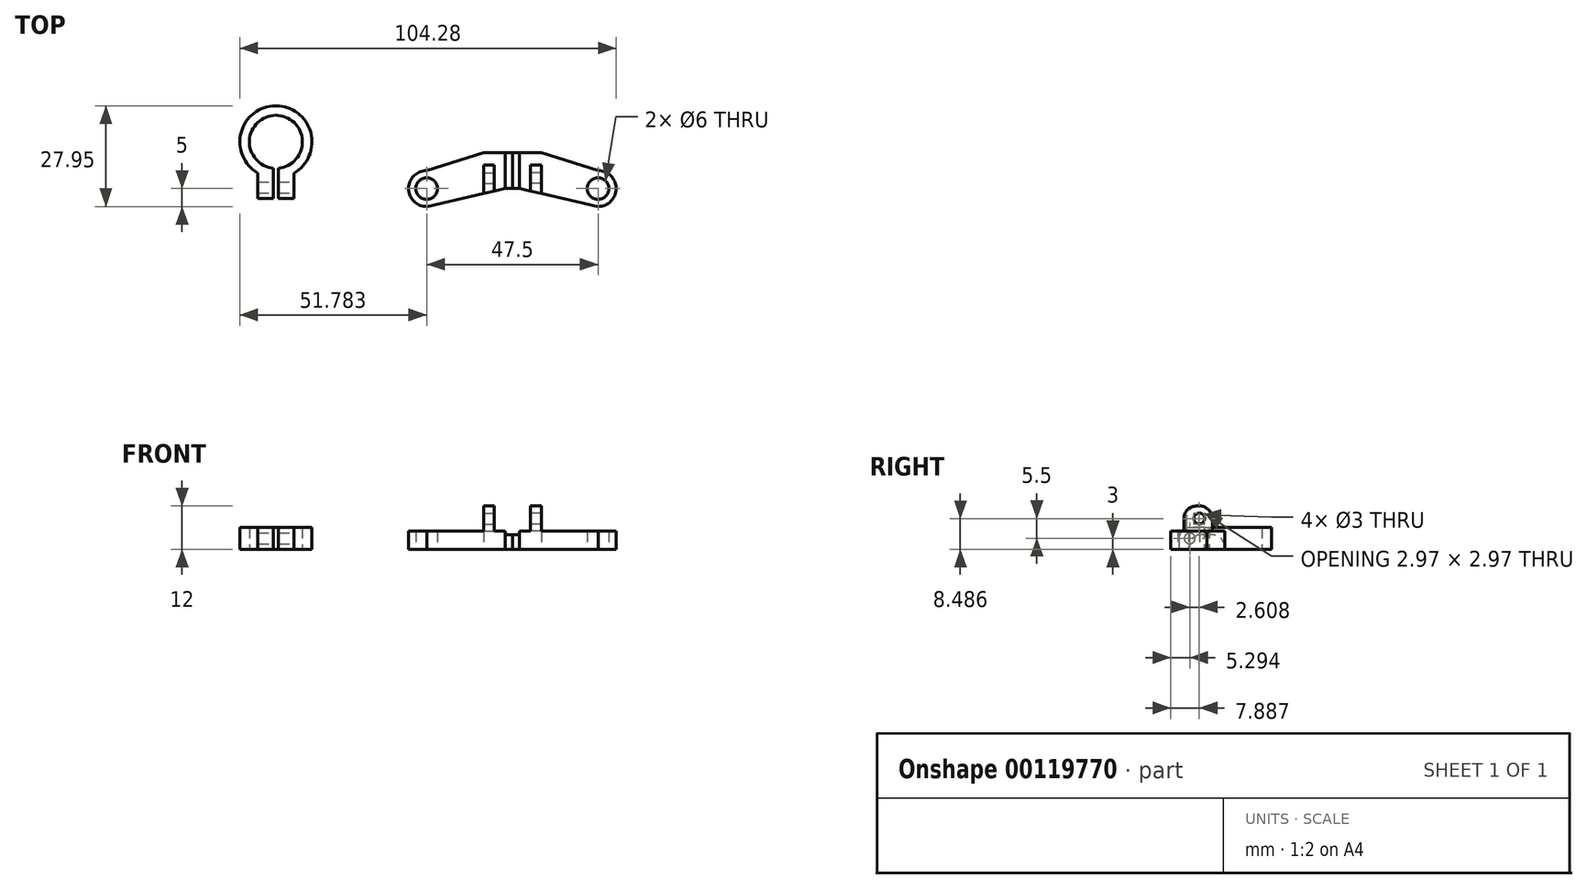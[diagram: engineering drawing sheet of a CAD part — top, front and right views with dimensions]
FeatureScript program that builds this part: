
annotation { "Feature Type Name" : "Feature", "Feature Type Description" : "" }
export const myFeature = defineFeature(function(context is Context, id is Id, definition is map)
    precondition{}
    {
        {
            var Q0;
            Q0=qCreatedBy(makeId("Top.planeOp"),FACE);
            var sketch = newSketch(context, id + "F0", { "sketchPlane" : qUnion([Q0])});
            skCircle(sketch, "E0", {"center": v(-31.45, 17.95) * mm, "radius": 7.35 * mm});
            skCircle(sketch, "E1", {"center": v(-31.45, 17.95) * mm, "radius": 10 * mm});
            skLineSegment(sketch, "E2", {"start": v(-26.45, 9.3) * mm, "end": v(-26.45, 2.3) * mm});
            skLineSegment(sketch, "E3", {"start": v(-26.45, 2.3) * mm, "end": v(-36.45, 2.3) * mm});
            skLineSegment(sketch, "E4", {"start": v(-36.45, 2.3) * mm, "end": v(-36.45, 9.3) * mm});
            skLineSegment(sketch, "E5", {"start": v(-32.15, 2.3) * mm, "end": v(-32.15, 10.64) * mm});
            skLineSegment(sketch, "E6", {"start": v(-30.75, 2.3) * mm, "end": v(-30.75, 10.64) * mm});
            skSolve(sketch);
        }
        {
            var Q0;
            {var subQ0=sQuery(id+"F0.wireOp",EDGE,"E2");Q0=makeQuery(id+"F0.imprint","IMPRINT",FACE,{"disambiguationData":[TD([[makeQuery(id+"F0.imprint","IMPRINT",EDGE,{"derivedFrom":subQ0}),-1.0]])]});}
            var Q1;
            {var subQ0=sQuery(id+"F0.wireOp",EDGE,"E4");Q1=makeQuery(id+"F0.imprint","IMPRINT",FACE,{"disambiguationData":[TD([[makeQuery(id+"F0.imprint","IMPRINT",EDGE,{"derivedFrom":subQ0}),-1.0]])]});}
            var Q2;
            {var subQ3=sQuery(id+"F0.wireOp",EDGE,"E5");var subQ4=sQuery(id+"F0.wireOp",EDGE,"E0");var subQ5=makeQuery(id+"F0.imprint","INTERSECT",VERTEX,{"derivedFrom":[subQ4,subQ3]});Q2=makeQuery(id+"F0.imprint","IMPRINT",FACE,{"disambiguationData":[TD([[makeQuery(id+"F0.imprint","IMPRINT",EDGE,{"disambiguationData":[TD([[subQ5,1.0]])],"derivedFrom":subQ4}),-1.0]])]});}
            extrude(context, id + "F1", {"entities" : qUnion([Q0, Q1, Q2]), "depth" : 6 * mm});
        }
        {
            var Q0;
            Q0=makeQuery(id+"F1.opExtrude","SWEPT_FACE",FACE,{"disambiguationData":[OSD([sQuery(id+"F0.wireOp",EDGE,"E2")])]});
            var sketch = newSketch(context, id + "F2", { "sketchPlane" : qUnion([Q0])});
            skPoint(sketch, "E7", {"position": v(5.3, 3) * mm});
            skSolve(sketch);
        }
        {
            var Q0;
            Q0=sQuery(id+"F2.wireOp",VERTEX,"E7");
            var Q1;
            Q1=makeQuery(id+"F1.opExtrude","SWEPT_BODY",BODY,{"disambiguationData":[OSD([sQuery(id+"F0.wireOp",EDGE,"E0"),sQuery(id+"F0.wireOp",EDGE,"E1"),sQuery(id+"F0.wireOp",EDGE,"E2"),sQuery(id+"F0.wireOp",EDGE,"E3"),sQuery(id+"F0.wireOp",EDGE,"E4")])]});
            hole(context, id + "F3", {"style" : HoleStyle.SIMPLE, "endStyle" : HoleEndStyle.THROUGH, "holeDiameter" : 3 * mm, "locations" : qUnion([Q0]), "scope" : qUnion([Q1]), "isTappedThrough" : true});
        }
        {
            var Q0;
            Q0=qCreatedBy(makeId("Top.planeOp"),FACE);
            var sketch = newSketch(context, id + "F4", { "sketchPlane" : qUnion([Q0])});
            skCircle(sketch, "E8", {"center": v(10.33, 5) * mm, "radius": 3 * mm});
            skLineSegment(sketch, "E9.left", {"start": v(5.33, 10) * mm, "end": v(5.33, 0) * mm});
            skPoint(sketch, "E10", {"position": v(10.33, 0) * mm});
            skPoint(sketch, "E11", {"position": v(34.08, 5) * mm});
            skLineSegment(sketch, "E12", {"start": v(34.08, 5) * mm, "end": v(32.08, 5) * mm});
            skLineSegment(sketch, "E13", {"start": v(32.08, 5) * mm, "end": v(10.33, 0) * mm});
            skPoint(sketch, "E14", {"position": v(29.08, 5) * mm});
            skPoint(sketch, "E15", {"position": v(26.08, 5) * mm});
            skLineSegment(sketch, "E16", {"start": v(26.08, 5) * mm, "end": v(26.08, 15) * mm});
            skLineSegment(sketch, "E17", {"start": v(34.08, 15) * mm, "end": v(26.08, 15) * mm});
            skLineSegment(sketch, "E18", {"start": v(29.08, 5) * mm, "end": v(29.08, 15) * mm});
            skPoint(sketch, "E19", {"position": v(32.08, 15) * mm});
            skLineSegment(sketch, "E20", {"start": v(32.08, 5) * mm, "end": v(32.08, 5) * mm});
            skPoint(sketch, "E21", {"position": v(10.33, 10) * mm});
            skLineSegment(sketch, "E22", {"start": v(32.08, 15) * mm, "end": v(32.08, 5) * mm});
            skLineSegment(sketch, "E23", {"start": v(5.33, 10) * mm, "end": v(10.33, 10) * mm});
            skLineSegment(sketch, "E24", {"start": v(5.33, 0) * mm, "end": v(10.33, 0) * mm});
            skLineSegment(sketch, "E25", {"start": v(34.08, 5) * mm, "end": v(34.08, 15) * mm});
            skLineSegment(sketch, "E26", {"start": v(10.33, 10) * mm, "end": v(26.08, 15) * mm});
            skPoint(sketch, "E27", {"position": v(26.08, 11.5) * mm});
            skLineSegment(sketch, "E28", {"start": v(26.08, 11.5) * mm, "end": v(29.08, 11.5) * mm});
            skLineSegment(sketch, "E29", {"start": v(26.08, 5) * mm, "end": v(26.08, 3.62) * mm});
            skLineSegment(sketch, "E30", {"start": v(29.08, 5) * mm, "end": v(29.08, 4.31) * mm});
            skSolve(sketch);
        }
        {
            var Q0;
            {var subQ2=sQuery(id+"F4.wireOp",EDGE,"E28");Q0=makeQuery(id+"F4.imprint","IMPRINT",FACE,{"disambiguationData":[TD([[makeQuery(id+"F4.imprint","IMPRINT",EDGE,{"derivedFrom":subQ2}),-1.0]])]});}
            extrude(context, id + "F5", {"entities" : qUnion([Q0]), "depth" : 12 * mm});
        }
        {
            var Q0;
            Q0=makeQuery(id+"F4.imprint","IMPRINT",FACE,{"disambiguationData":[TD([[makeQuery(id+"F4.imprint","IMPRINT",EDGE,{"derivedFrom":sQuery(id+"F4.wireOp",EDGE,"E8")}),-1.0]])]});
            var Q1;
            {var subQ0=sQuery(id+"F4.wireOp",EDGE,"E18");Q1=makeQuery(id+"F4.imprint","IMPRINT",FACE,{"disambiguationData":[TD([[makeQuery(id+"F4.imprint","IMPRINT",EDGE,{"derivedFrom":subQ0}),-1.0]])]});}
            var Q2;
            {var subQ3=sQuery(id+"F4.wireOp",EDGE,"1xFQyo0G-Xs1s-Fqlw-DN10-UjsStAcqlzeH");Q2=makeQuery(id+"F4.imprint","IMPRINT",FACE,{"disambiguationData":[TD([[makeQuery(id+"F4.imprint","IMPRINT",EDGE,{"derivedFrom":subQ3}),1.0]])]});}
            var Q3;
            {var subQ3=sQuery(id+"F4.wireOp",EDGE,"E28");Q3=makeQuery(id+"F4.imprint","IMPRINT",FACE,{"disambiguationData":[TD([[makeQuery(id+"F4.imprint","IMPRINT",EDGE,{"derivedFrom":subQ3}),1.0]])]});}
            extrude(context, id + "F6", {"entities" : qUnion([Q0, Q1, Q2, Q3]), "operationType" : NewBodyOperationType.ADD, "depth" : 5 * mm});
        }
        {
            var Q0;
            {var subQ3=sQuery(id+"F4.wireOp",EDGE,"uUS1zDU1-sOwB-zFEP-Xbho-WG0gHNYcOc71");Q0=makeQuery(id+"F4.imprint","IMPRINT",FACE,{"disambiguationData":[TD([[makeQuery(id+"F4.imprint","IMPRINT",EDGE,{"derivedFrom":subQ3}),-1.0]])]});}
            var Q1;
            {var subQ4=sQuery(id+"F4.wireOp",EDGE,"E12");Q1=makeQuery(id+"F4.imprint","IMPRINT",FACE,{"disambiguationData":[TD([[makeQuery(id+"F4.imprint","IMPRINT",EDGE,{"derivedFrom":subQ4}),-1.0]])]});}
            var Q2;
            {var subQ1=sQuery(id+"F4.wireOp",EDGE,"N1TZ5UtL-Frhi-5IxH-qIdc-fXHmOs3rLAIg");Q2=makeQuery(id+"F4.imprint","IMPRINT",FACE,{"disambiguationData":[TD([[makeQuery(id+"F4.imprint","IMPRINT",EDGE,{"derivedFrom":subQ1}),1.0]])]});}
            extrude(context, id + "F7", {"entities" : qUnion([Q0, Q1, Q2]), "operationType" : NewBodyOperationType.ADD, "depth" : 4 * mm});
        }
        {
            var Q0;
            Q0=makeQuery(id+"F6.opExtrude","SWEPT_EDGE",EDGE,{"disambiguationData":[OSD([sQuery(id+"F4.wireOp",EDGE,"E9.top"),sQuery(id+"F4.wireOp",EDGE,"E9.left")])]});
            var Q1;
            Q1=makeQuery(id+"F6.opExtrude","SWEPT_EDGE",EDGE,{"disambiguationData":[OSD([sQuery(id+"F4.wireOp",EDGE,"E9.bottom"),sQuery(id+"F4.wireOp",EDGE,"E9.left")])]});
            fillet(context, id + "F8", {"entities" : qUnion([Q0, Q1]), "radius" : 5 * mm, "tangentPropagation" : true, "allowEdgeOverflow" : false});
        }
        {
            var Q0;
            {var subQ0=makeQuery(id+"F7.opExtrude","CAP_EDGE",EDGE,{"disambiguationData":[OSD([sQuery(id+"F4.wireOp",EDGE,"E17")])],"isStart":false});Q0=makeQuery(id+"F12.boolean.opBoolean","MERGE",EDGE,{"derivedFrom":[subQ0,makeQuery(id+"F12.opPattern","COPY",EDGE,{"derivedFrom":subQ0,"instanceName":"1"})]});}
            var Q1;
            {var subQ0=makeQuery(id+"F7.opExtrude","CAP_EDGE",EDGE,{"disambiguationData":[OSD([sQuery(id+"F4.wireOp",EDGE,"E12")])],"isStart":false});Q1=makeQuery(id+"F12.boolean.opBoolean","MERGE",EDGE,{"derivedFrom":[subQ0,makeQuery(id+"F12.opPattern","COPY",EDGE,{"derivedFrom":subQ0,"instanceName":"1"})]});}
            var Q2;
            Q2=makeQuery(id+"F5.opExtrude","CAP_EDGE",EDGE,{"disambiguationData":[OSD([sQuery(id+"F4.wireOp",EDGE,"E17")])],"isStart":false});
            var Q3;
            Q3=makeQuery(id+"F5.opExtrude","CAP_EDGE",EDGE,{"disambiguationData":[OSD([sQuery(id+"F4.wireOp",EDGE,"E9.bottom")])],"isStart":false});
            var Q4;
            Q4=makeQuery(id+"F5.opExtrude","CAP_EDGE",EDGE,{"disambiguationData":[OSD([sQuery(id+"F4.wireOp",EDGE,"5s7RhZCa-M1fr-UkVQ-8m6s-rdF7uYrRGpCK")])],"isStart":false});
            var Q5;
            Q5=makeQuery(id+"F5.opExtrude","CAP_EDGE",EDGE,{"disambiguationData":[OSD([sQuery(id+"F4.wireOp",EDGE,"E28")])],"isStart":false});
            var Q6;
            Q6=makeQuery(id+"F5.opExtrude","CAP_EDGE",EDGE,{"disambiguationData":[OSD([sQuery(id+"F4.wireOp",EDGE,"E13")])],"isStart":false});
            fillet(context, id + "F9", {"entities" : qUnion([Q0, Q1, Q2, Q3, Q4, Q5, Q6]), "radius" : 3.5 * mm, "tangentPropagation" : true, "allowEdgeOverflow" : false});
        }
        {
            var Q0;
            Q0=makeQuery(id+"F5.opExtrude","SWEPT_FACE",FACE,{"disambiguationData":[OSD([sQuery(id+"F4.wireOp",EDGE,"E18"),sQuery(id+"F4.wireOp",EDGE,"E30")])]});
            var sketch = newSketch(context, id + "F10", { "sketchPlane" : qUnion([Q0])});
            skPoint(sketch, "E31", {"position": v(7.9, 8.5) * mm});
            skSolve(sketch);
        }
        {
            var Q0;
            Q0=sQuery(id+"F10.wireOp",VERTEX,"E31");
            var Q1;
            Q1=makeQuery(id+"F5.opExtrude","SWEPT_BODY",BODY,{"disambiguationData":[OSD([sQuery(id+"F4.wireOp",EDGE,"E9.bottom"),sQuery(id+"F4.wireOp",EDGE,"E16"),sQuery(id+"F4.wireOp",EDGE,"E17"),sQuery(id+"F4.wireOp",EDGE,"E18")])]});
            hole(context, id + "F11", {"style" : HoleStyle.SIMPLE, "endStyle" : HoleEndStyle.THROUGH, "holeDiameter" : 3 * mm, "locations" : qUnion([Q0]), "scope" : qUnion([Q1]), "isTappedThrough" : true});
        }
        {
            var Q0;
            Q0=makeQuery(id+"F5.opExtrude","SWEPT_BODY",BODY,{"disambiguationData":[OSD([sQuery(id+"F4.wireOp",EDGE,"E9.bottom"),sQuery(id+"F4.wireOp",EDGE,"E16"),sQuery(id+"F4.wireOp",EDGE,"E17"),sQuery(id+"F4.wireOp",EDGE,"E18")])]});
            var Q1;
            Q1=makeQuery(id+"F7.opExtrude","SWEPT_FACE",FACE,{"disambiguationData":[OSD([sQuery(id+"F4.wireOp",EDGE,"E25")])]});
            mirror(context, id + "F12", {"operationType" : NewBodyOperationType.ADD, "entities" : qUnion([Q0]), "mirrorPlane" : qUnion([Q1])});
        }
        {
            var Q0;
            {var subQ0=sQuery(id+"F0.wireOp",EDGE,"E3");Q0=makeQuery(id+"F1.opExtrude","CAP_EDGE",EDGE,{"disambiguationData":[OSD([subQ0]),TDD([makeQuery(id+"F0.imprint","IMPRINT",EDGE,{"disambiguationData":[TD([[makeQuery(id+"F0.imprint","INTERSECT",VERTEX,{"derivedFrom":[subQ0,sQuery(id+"F0.wireOp",EDGE,"E4")]}),1.0]])],"derivedFrom":subQ0})])],"isStart":false});}
            var Q1;
            {var subQ0=sQuery(id+"F0.wireOp",EDGE,"E3");Q1=makeQuery(id+"F1.opExtrude","CAP_EDGE",EDGE,{"disambiguationData":[OSD([subQ0]),TDD([makeQuery(id+"F0.imprint","IMPRINT",EDGE,{"disambiguationData":[TD([[makeQuery(id+"F0.imprint","INTERSECT",VERTEX,{"derivedFrom":[sQuery(id+"F0.wireOp",EDGE,"E2"),subQ0]}),-1.0]])],"derivedFrom":subQ0})])],"isStart":false});}
            fillet(context, id + "F13", {"entities" : qUnion([Q0, Q1]), "radius" : 3 * mm, "tangentPropagation" : true, "allowEdgeOverflow" : false});
        }
    });
